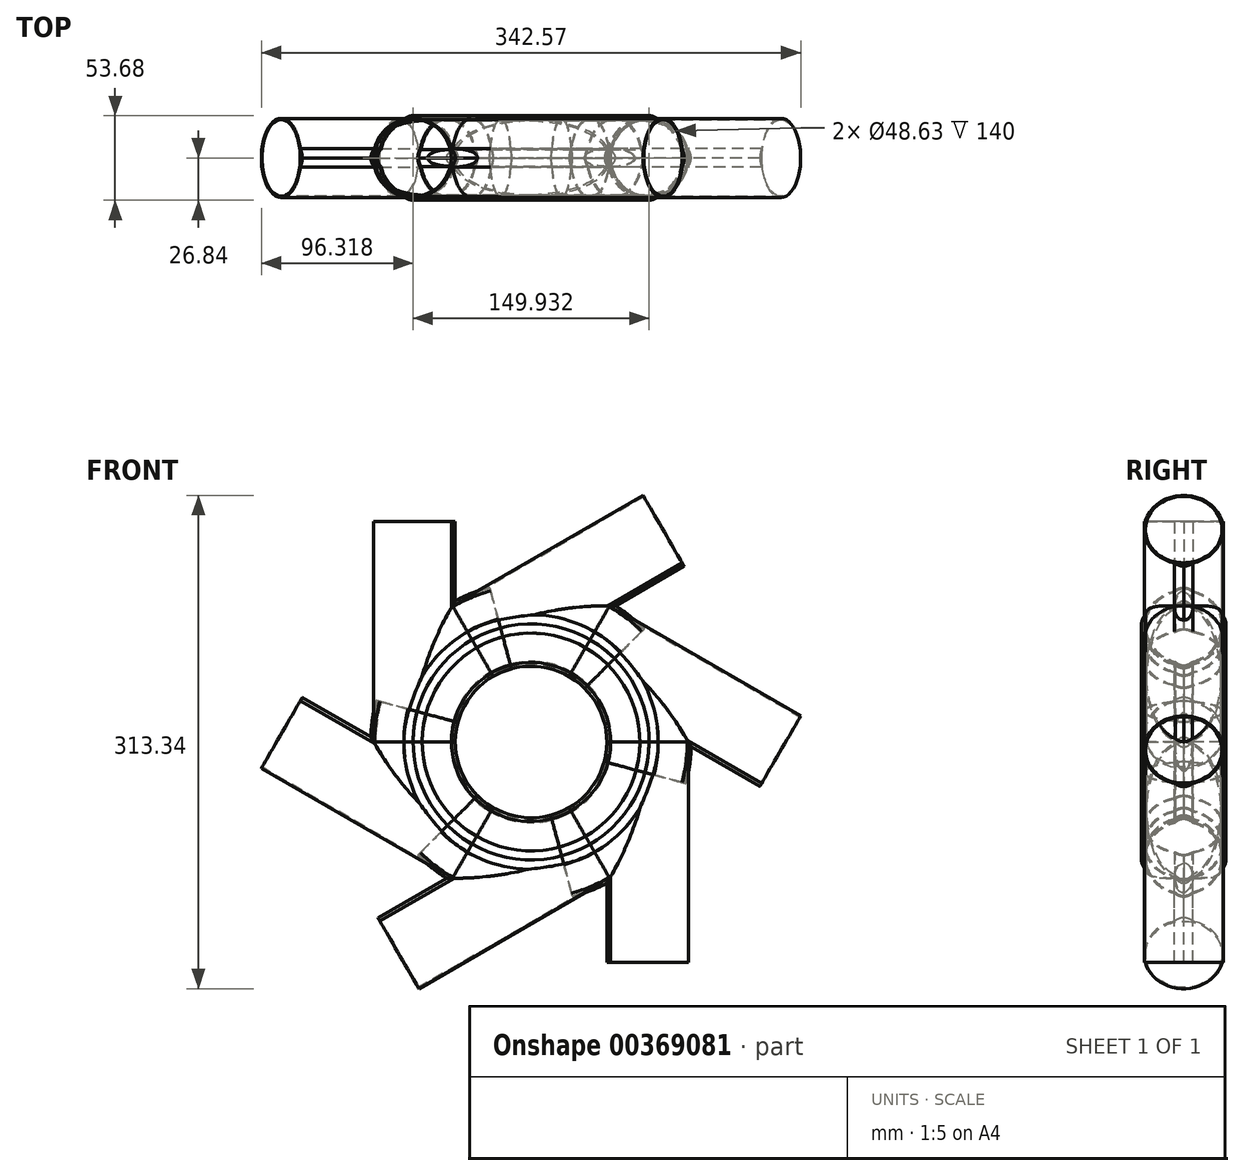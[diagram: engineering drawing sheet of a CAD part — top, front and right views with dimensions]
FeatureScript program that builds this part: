
annotation { "Feature Type Name" : "Feature", "Feature Type Description" : "" }
export const myFeature = defineFeature(function(context is Context, id is Id, definition is map)
    precondition{}
    {
        {
            var Q0;
            Q0=qCreatedBy(makeId("Top.planeOp"),FACE);
            var sketch = newSketch(context, id + "F0", { "sketchPlane" : qUnion([Q0])});
            skCircle(sketch, "E0", {"center": v(0, 0) * mm, "radius": 25.12 * mm});
            skArc(sketch, "E1", {"start": v(-26.84, 0) * mm, "mid": v(-26.18, -3.14) * mm, "end": v(-24.43, -5.84) * mm});
            skArc(sketch, "E2.MirrorCS", {"start": v(-26.84, 0) * mm, "mid": v(-26.18, 3.14) * mm, "end": v(-24.43, 5.84) * mm});
            skArc(sketch, "E3.1.0", {"start": v(0, -26.84) * mm, "mid": v(-3.14, -26.18) * mm, "end": v(-5.84, -24.43) * mm});
            skArc(sketch, "E3.1.1", {"start": v(0, -26.84) * mm, "mid": v(3.14, -26.18) * mm, "end": v(5.84, -24.43) * mm});
            skArc(sketch, "E3.2.0", {"start": v(26.84, 0) * mm, "mid": v(26.18, -3.14) * mm, "end": v(24.43, -5.84) * mm});
            skArc(sketch, "E3.2.1", {"start": v(26.84, 0) * mm, "mid": v(26.18, 3.14) * mm, "end": v(24.43, 5.84) * mm});
            skArc(sketch, "E3.3.0", {"start": v(0, 26.84) * mm, "mid": v(3.14, 26.18) * mm, "end": v(5.84, 24.43) * mm});
            skArc(sketch, "E3.3.1", {"start": v(0, 26.84) * mm, "mid": v(-3.14, 26.18) * mm, "end": v(-5.84, 24.43) * mm});
            skLineSegment(sketch, "E4", {"start": v(-74.97, -31.74) * mm, "end": v(-74.97, 32) * mm});
            skSolve(sketch);
        }
        {
            var Q0;
            Q0 = qSketchRegion(id + "F0", true);
            var Q1;
            Q1=sQuery(id+"F0.wireOp",EDGE,"E4");
            revolve(context, id + "F1", {"entities" : qUnion([Q0]), "axis" : qUnion([Q1]), "revolveType" : RevolveType.ONE_DIRECTION, "angle" : 75 * degree});
        }
        {
            var Q0;
            {var subQ0=sQuery(id+"F0.wireOp",EDGE,"E0");var subQ5=makeQuery(id+"F0.imprint","INTERSECT",VERTEX,{"derivedFrom":[subQ0,sQuery(id+"F0.wireOp",EDGE,"E3.2.1")]});Q0=makeQuery(id+"F0.imprint","IMPRINT",FACE,{"disambiguationData":[TD([[makeQuery(id+"F0.imprint","IMPRINT",EDGE,{"disambiguationData":[TD([[subQ5,-1.0]])],"derivedFrom":subQ0}),1.0]])]});}
            var Q1;
            {var subQ0=sQuery(id+"F0.wireOp",EDGE,"E3.2.0");Q1=makeQuery(id+"F0.imprint","IMPRINT",FACE,{"disambiguationData":[TD([[makeQuery(id+"F0.imprint","IMPRINT",EDGE,{"derivedFrom":subQ0}),-1.0]])]});}
            var Q2;
            {var subQ0=sQuery(id+"F0.wireOp",EDGE,"E3.3.0");Q2=makeQuery(id+"F0.imprint","IMPRINT",FACE,{"disambiguationData":[TD([[makeQuery(id+"F0.imprint","IMPRINT",EDGE,{"derivedFrom":subQ0}),-1.0]])]});}
            var Q3;
            {var subQ0=sQuery(id+"F0.wireOp",EDGE,"E1");Q3=makeQuery(id+"F0.imprint","IMPRINT",FACE,{"disambiguationData":[TD([[makeQuery(id+"F0.imprint","IMPRINT",EDGE,{"derivedFrom":subQ0}),1.0]])]});}
            var Q4;
            {var subQ0=sQuery(id+"F0.wireOp",EDGE,"E3.1.0");Q4=makeQuery(id+"F0.imprint","IMPRINT",FACE,{"disambiguationData":[TD([[makeQuery(id+"F0.imprint","IMPRINT",EDGE,{"derivedFrom":subQ0}),-1.0]])]});}
            var Q5;
            Q5 = qConstructionFilter(qBodyType(qCreatedBy(id + "F0" ,EDGE), BodyType.WIRE), ConstructionObject.NO);
            extrude(context, id + "F2", {"entities" : qUnion([Q0, Q1, Q2, Q3, Q4]), "operationType" : NewBodyOperationType.ADD, "surfaceEntities" : qUnion([Q5]), "oppositeDirection" : true, "depth" : 140 * mm});
        }
        {
            var Q0;
            Q0=makeQuery(id+"F2.opExtrude","CAP_FACE",FACE,{"disambiguationData":[OSD([sQuery(id+"F0.wireOp",EDGE,"E0"),sQuery(id+"F0.wireOp",EDGE,"E1"),sQuery(id+"F0.wireOp",EDGE,"E2.MirrorCS"),sQuery(id+"F0.wireOp",EDGE,"E3.1.0"),sQuery(id+"F0.wireOp",EDGE,"E3.1.1"),sQuery(id+"F0.wireOp",EDGE,"E3.2.0"),sQuery(id+"F0.wireOp",EDGE,"E3.2.1"),sQuery(id+"F0.wireOp",EDGE,"E3.3.0"),sQuery(id+"F0.wireOp",EDGE,"E3.3.1")])],"isStart":false});
            var sketch = newSketch(context, id + "F3", { "sketchPlane" : qUnion([Q0])});
            skCircle(sketch, "E5.0", {"center": v(0, 0) * mm, "radius": 24.32 * mm});
            skSolve(sketch);
        }
        {
            var Q0;
            Q0 = qSketchRegion(id + "F3", true);
            extrude(context, id + "F4", {"entities" : qUnion([Q0]), "operationType" : NewBodyOperationType.REMOVE, "oppositeDirection" : true, "depth" : 206 * mm});
        }
        {
            var Q0;
            Q0=makeQuery(id+"F1.opRevolve","CAP_FACE",FACE,{"disambiguationData":[OSD([sQuery(id+"F0.wireOp",EDGE,"E0"),sQuery(id+"F0.wireOp",EDGE,"E1"),sQuery(id+"F0.wireOp",EDGE,"E2.MirrorCS"),sQuery(id+"F0.wireOp",EDGE,"E3.1.0"),sQuery(id+"F0.wireOp",EDGE,"E3.1.1"),sQuery(id+"F0.wireOp",EDGE,"E3.2.0"),sQuery(id+"F0.wireOp",EDGE,"E3.2.1"),sQuery(id+"F0.wireOp",EDGE,"E3.3.0"),sQuery(id+"F0.wireOp",EDGE,"E3.3.1")])],"isStart":false});
            var sketch = newSketch(context, id + "F5", { "sketchPlane" : qUnion([Q0])});
            skArc(sketch, "E6.0", {"start": v(-5.44, -31.86) * mm, "mid": v(-17.2, -38.37) * mm, "end": v(-23.7, -50.13) * mm});
            skArc(sketch, "E6.1", {"start": v(0, -81.6) * mm, "mid": v(2.94, -80.96) * mm, "end": v(5.44, -79.26) * mm});
            skArc(sketch, "E6.2", {"start": v(-5.44, -79.26) * mm, "mid": v(-2.94, -80.96) * mm, "end": v(0, -81.6) * mm});
            skArc(sketch, "E6.3", {"start": v(-23.7, -61) * mm, "mid": v(-17.2, -72.76) * mm, "end": v(-5.44, -79.26) * mm});
            skArc(sketch, "E6.4", {"start": v(-26.04, -55.56) * mm, "mid": v(-25.4, -58.5) * mm, "end": v(-23.7, -61) * mm});
            skArc(sketch, "E6.5", {"start": v(5.44, -79.26) * mm, "mid": v(17.2, -72.76) * mm, "end": v(23.7, -61) * mm});
            skArc(sketch, "E6.6", {"start": v(-23.7, -50.13) * mm, "mid": v(-25.4, -52.62) * mm, "end": v(-26.04, -55.56) * mm});
            skArc(sketch, "E6.7", {"start": v(23.7, -61) * mm, "mid": v(25.4, -58.5) * mm, "end": v(26.04, -55.56) * mm});
            skArc(sketch, "E6.8", {"start": v(26.04, -55.56) * mm, "mid": v(25.4, -52.62) * mm, "end": v(23.7, -50.13) * mm});
            skArc(sketch, "E6.9", {"start": v(23.7, -50.13) * mm, "mid": v(17.2, -38.37) * mm, "end": v(5.44, -31.86) * mm});
            skArc(sketch, "E6.10", {"start": v(5.44, -31.86) * mm, "mid": v(2.94, -30.17) * mm, "end": v(0, -29.53) * mm});
            skArc(sketch, "E6.11", {"start": v(0, -29.53) * mm, "mid": v(-2.94, -30.17) * mm, "end": v(-5.44, -31.86) * mm});
            skSolve(sketch);
        }
        {
            var Q0;
            Q0 = qSketchRegion(id + "F5", true);
            var Q1;
            Q1=sQuery(id+"F0.wireOp",EDGE,"E4");
            revolve(context, id + "F6", {"operationType" : NewBodyOperationType.REMOVE, "entities" : qUnion([Q0]), "axis" : qUnion([Q1]), "revolveType" : RevolveType.FULL, "oppositeDirection" : true});
        }
        {
            var Q0;
            Q0=makeQuery(id+"F1.opRevolve","SWEPT_BODY",BODY,{"disambiguationData":[OSD([sQuery(id+"F0.wireOp",EDGE,"E0"),sQuery(id+"F0.wireOp",EDGE,"E1"),sQuery(id+"F0.wireOp",EDGE,"E2.MirrorCS"),sQuery(id+"F0.wireOp",EDGE,"E3.1.0"),sQuery(id+"F0.wireOp",EDGE,"E3.1.1"),sQuery(id+"F0.wireOp",EDGE,"E3.2.0"),sQuery(id+"F0.wireOp",EDGE,"E3.2.1"),sQuery(id+"F0.wireOp",EDGE,"E3.3.0"),sQuery(id+"F0.wireOp",EDGE,"E3.3.1")])]});
            var Q1;
            Q1=sQuery(id+"F0.wireOp",EDGE,"E4");
            circularPattern(context, id + "F7", {"entities" : qUnion([Q0]), "axis" : qUnion([Q1]), "angle" : 360 * degree, "instanceCount" : 6, "equalSpace" : true});
        }
    });
